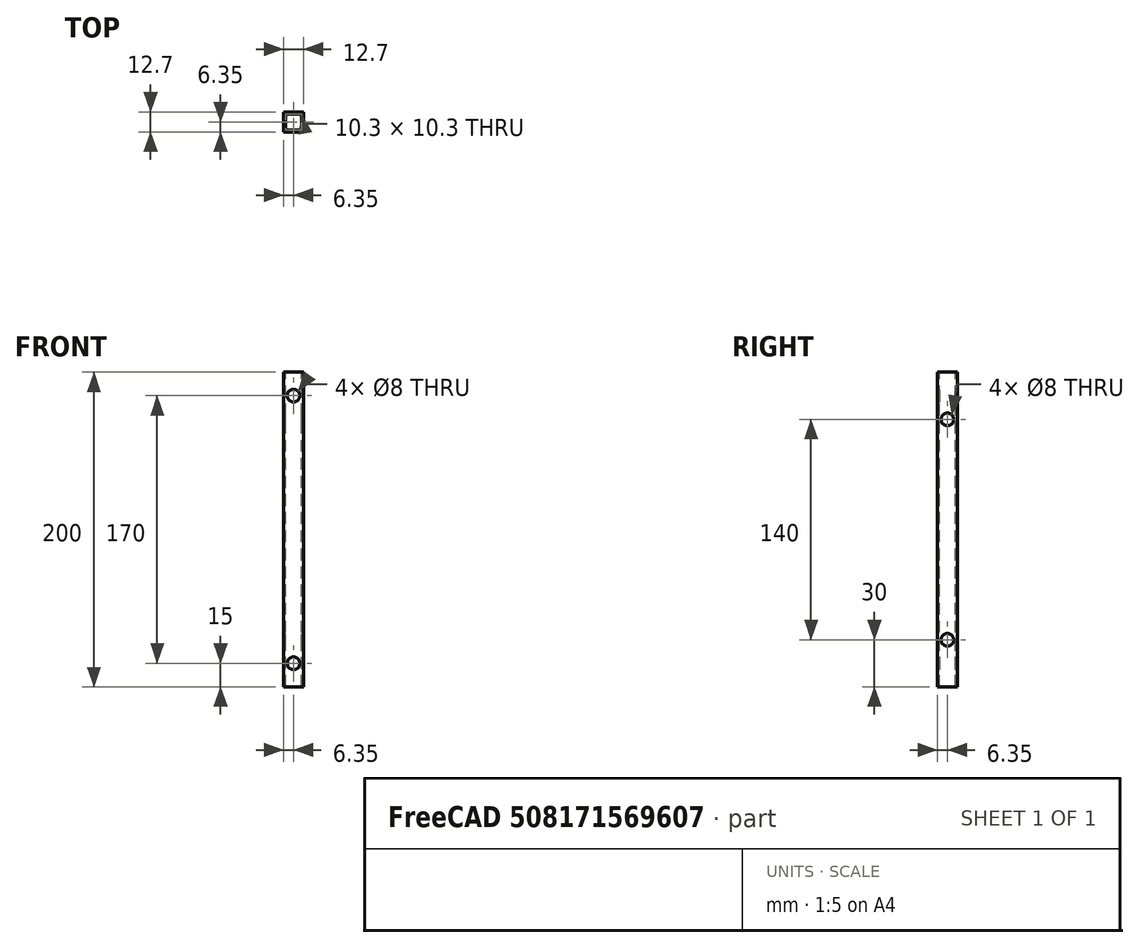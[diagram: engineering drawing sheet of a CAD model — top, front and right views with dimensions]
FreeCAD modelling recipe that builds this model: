
FCSTD DOCUMENT  (FreeCAD 0.18.4R)
Label: sp_posteBarrenado(alt20cm)(hoyosRad4mm)
License: All rights reserved
LicenseURL: http://en.wikipedia.org/wiki/All_rights_reserved
objects: Part::Cut×5, Part::Cylinder×4, Part::Box×2
note: 11 computed .brp shape members not serialized (recipe doc carries the construction recipe); baked Part::Feature solids carry a one-line shape summary decoded from their .brp

FEATURE [Part::Box] Box  label="cuboExterno"
  AttacherType = Attacher::AttachEngine3D
  Height = 200
  Length = 12.7
  Width = 12.7
FEATURE [Part::Box] Box001  label="cuboInterni"
  AttacherType = Attacher::AttachEngine3D
  Height = 200
  Length = 10.3
  Placement = pos=(1.2,1.2,0) rot=(0,0,1;0rad)
  Width = 10.3
FEATURE [Part::Cut] Cut  label="perfinSinBarrenos"
  Base = -> Box
  Tool = -> Box001
FEATURE [Part::Cylinder] Cylinder  label="Cilindro"
  Angle = 360
  AttacherType = Attacher::AttachEngine3D
  Height = 12.7
  Placement = pos=(6.35,0,15) rot=(1,0,0;4.71239rad)
  Radius = 4
FEATURE [Part::Cylinder] Cylinder001  label="Cilindro001"
  Angle = 360
  AttacherType = Attacher::AttachEngine3D
  Height = 12.7
  Placement = pos=(6.35,0,185) rot=(-1,0,0;1.5708rad)
  Radius = 4
FEATURE [Part::Cut] Cut001
  Base = -> Cut
  Tool = -> Cylinder001
FEATURE [Part::Cut] Cut002  label="dosBarrenos"
  Base = -> Cut001
  Tool = -> Cylinder
FEATURE [Part::Cylinder] Cylinder002  label="Cilindro002"
  Angle = 360
  AttacherType = Attacher::AttachEngine3D
  Height = 12.7
  Placement = pos=(0,6.35,30) rot=(0,1,0;1.5708rad)
  Radius = 4
FEATURE [Part::Cylinder] Cylinder003  label="Cilindro003"
  Angle = 360
  AttacherType = Attacher::AttachEngine3D
  Height = 12.7
  Placement = pos=(0,6.35,170) rot=(0,1,0;1.5708rad)
  Radius = 4
FEATURE [Part::Cut] Cut003
  Base = -> Cut002
  Tool = -> Cylinder002
FEATURE [Part::Cut] Cut004  label="posteBarrenado"
  Base = -> Cut003
  Tool = -> Cylinder003
